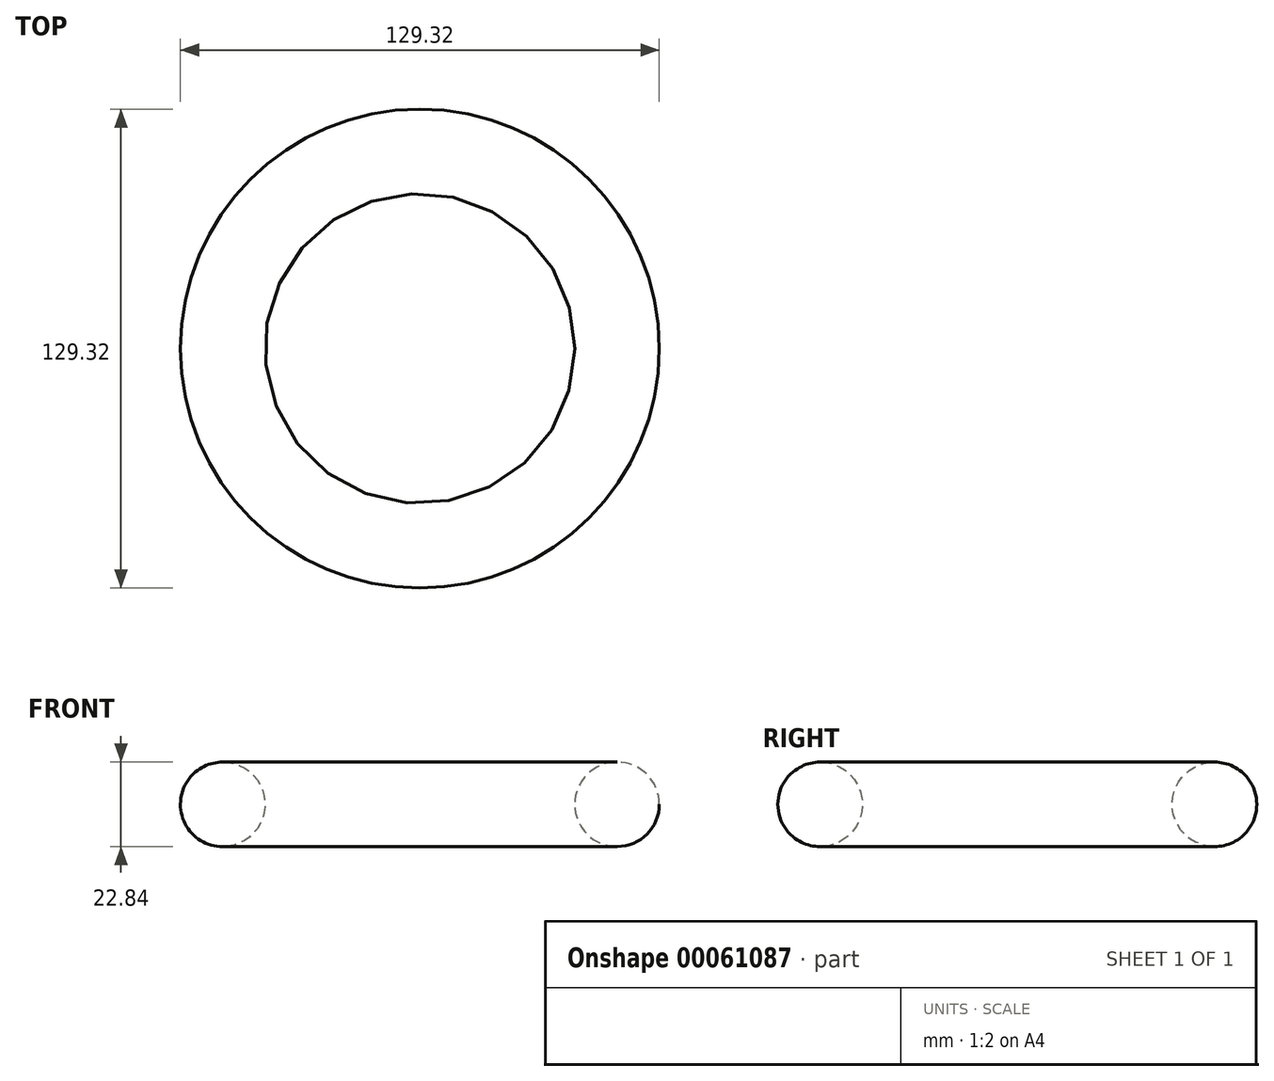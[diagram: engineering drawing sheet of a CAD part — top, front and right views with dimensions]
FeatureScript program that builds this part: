
annotation { "Feature Type Name" : "Feature", "Feature Type Description" : "" }
export const myFeature = defineFeature(function(context is Context, id is Id, definition is map)
    precondition{}
    {
        {
            var Q0;
            Q0=qCreatedBy(makeId("Front.planeOp"),FACE);
            var sketch = newSketch(context, id + "F0", { "sketchPlane" : qUnion([Q0])});
            skLineSegment(sketch, "E0", {"start": v(0, 41.42) * mm, "end": v(0, -48.3) * mm});
            skCircle(sketch, "E1", {"center": v(-53.24, 0) * mm, "radius": 11.42 * mm});
            skSolve(sketch);
        }
        {
            var Q0;
            Q0 = qSketchRegion(id + "F0", true);
            var Q1;
            Q1=sQuery(id+"F0.wireOp",EDGE,"E0");
            revolve(context, id + "F1", {"entities" : qUnion([Q0]), "axis" : qUnion([Q1]), "revolveType" : RevolveType.FULL});
        }
    });
